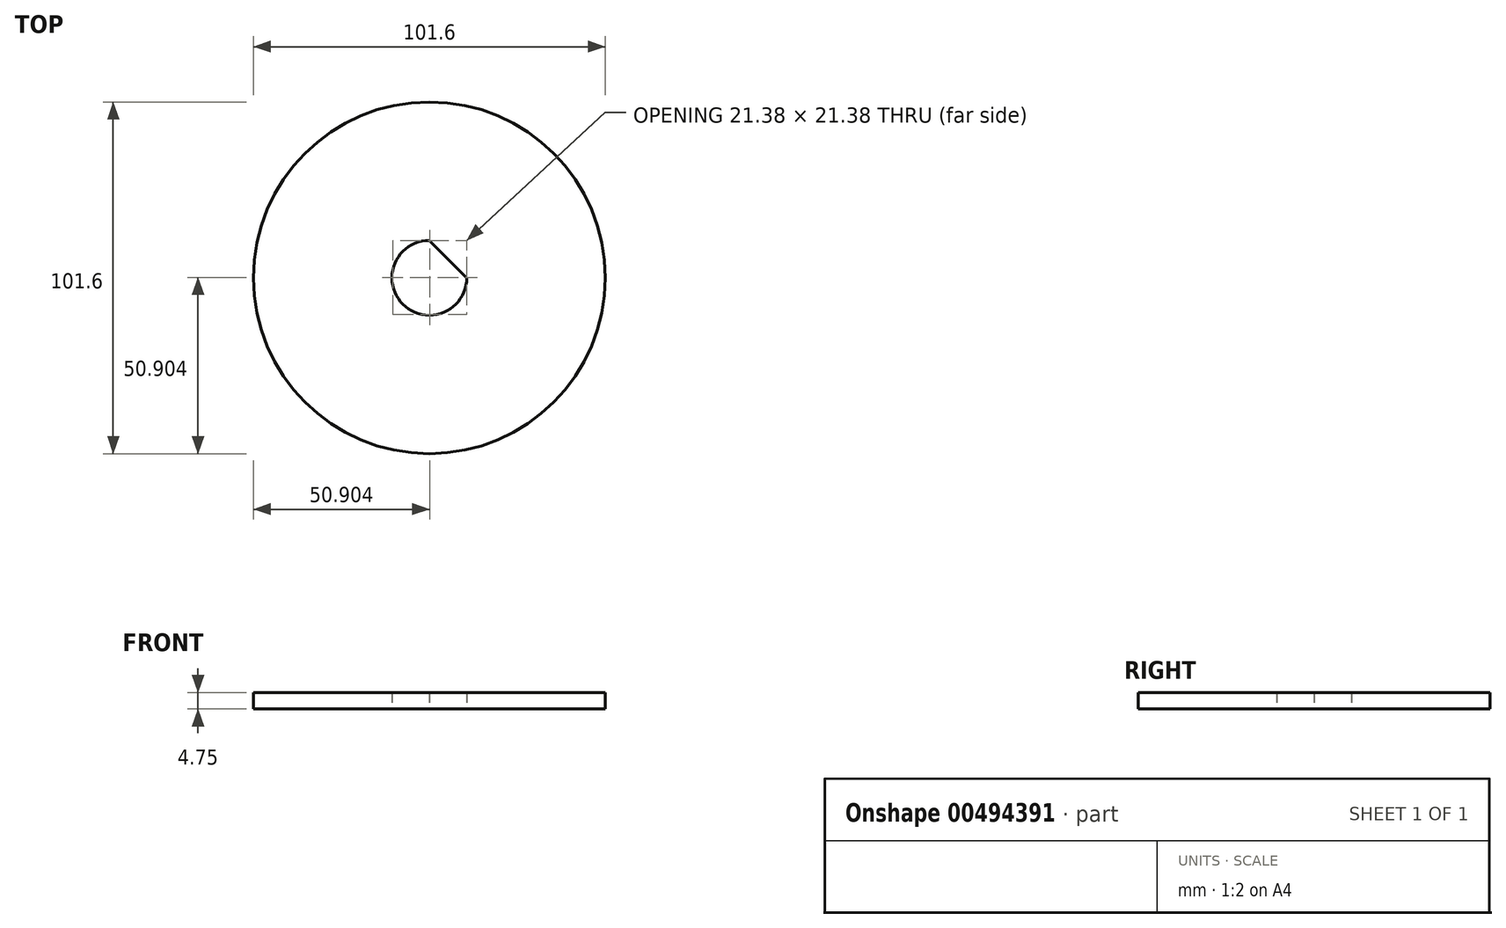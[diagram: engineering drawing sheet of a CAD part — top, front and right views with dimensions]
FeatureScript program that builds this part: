
annotation { "Feature Type Name" : "Feature", "Feature Type Description" : "" }
export const myFeature = defineFeature(function(context is Context, id is Id, definition is map)
    precondition{}
    {
        {
            var Q0;
            Q0=qCreatedBy(makeId("Top.planeOp"),FACE);
            var sketch = newSketch(context, id + "F0", { "sketchPlane" : qUnion([Q0])});
            skCircle(sketch, "E0", {"center": v(0, 0) * mm, "radius": 50.8 * mm});
            skArc(sketch, "E1", {"start": v(0, 10.8) * mm, "mid": v(-7.63, -7.63) * mm, "end": v(10.8, 0) * mm});
            skLineSegment(sketch, "E2", {"start": v(0, 10.8) * mm, "end": v(10.8, 0) * mm});
            skSolve(sketch);
        }
        {
            var Q0;
            Q0 = qSketchRegion(id + "F0", true);
            extrude(context, id + "F1", {"entities" : qUnion([Q0]), "depth" : 4.75 * mm});
        }
    });
